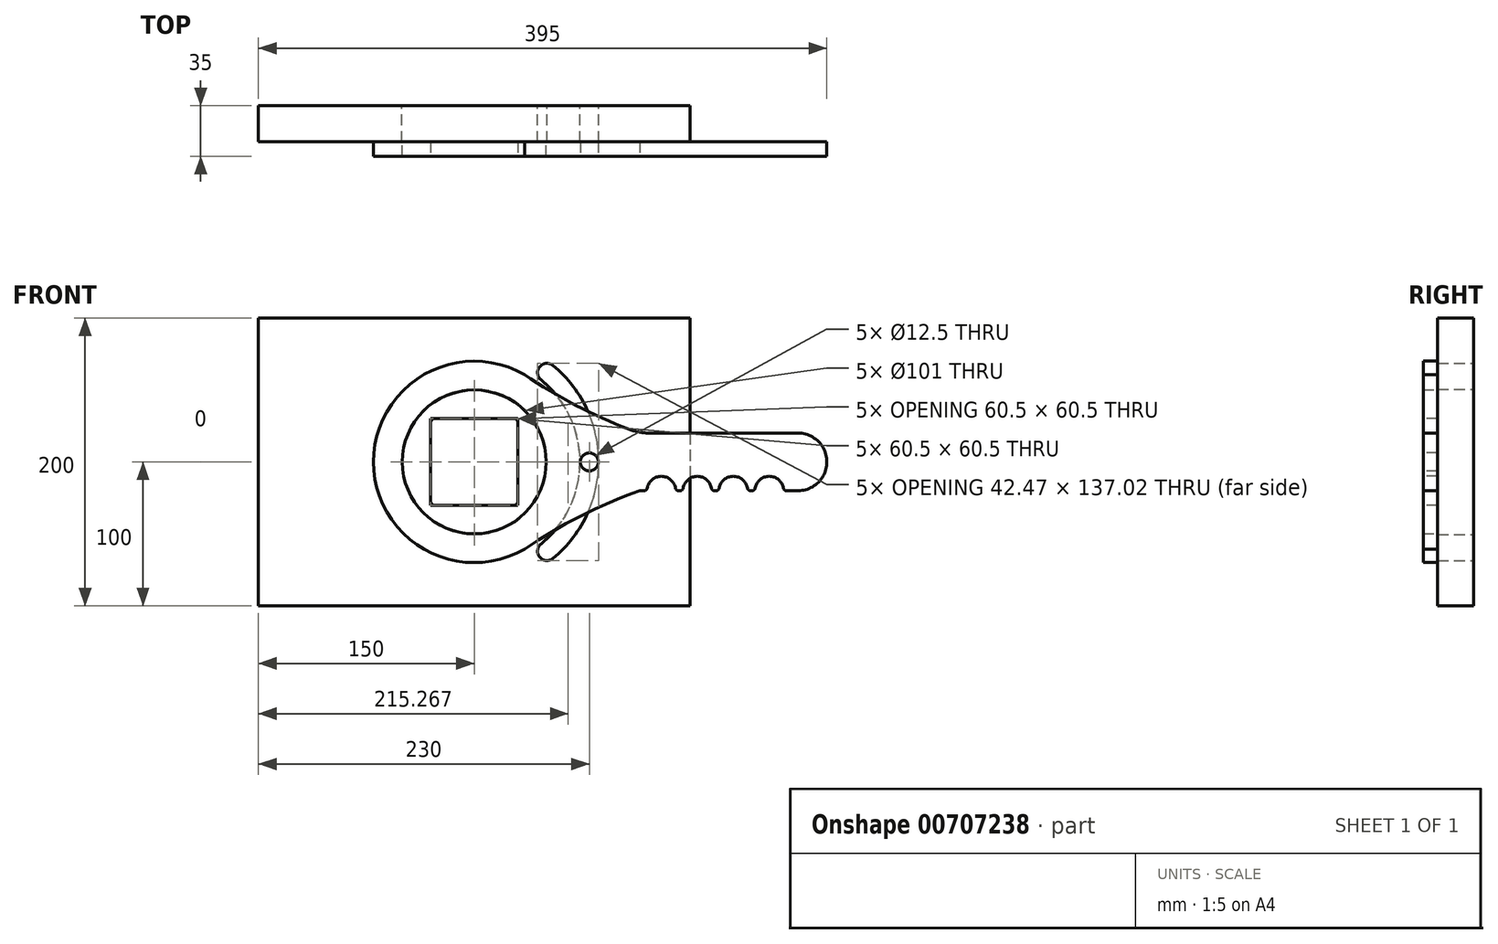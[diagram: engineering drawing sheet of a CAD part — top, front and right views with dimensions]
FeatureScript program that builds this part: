
annotation { "Feature Type Name" : "Feature", "Feature Type Description" : "" }
export const myFeature = defineFeature(function(context is Context, id is Id, definition is map)
    precondition{}
    {
        {
            var Q0;
            Q0=qCreatedBy(makeId("Front.planeOp"),FACE);
            var sketch = newSketch(context, id + "F0", { "sketchPlane" : qUnion([Q0])});
            skCircle(sketch, "E0.0", {"center": v(0, 0) * mm, "radius": 50.5 * mm});
            skLineSegment(sketch, "E1.bottom", {"start": v(150, 100) * mm, "end": v(-150, 100) * mm});
            skLineSegment(sketch, "E1.top", {"start": v(150, -100) * mm, "end": v(-150, -100) * mm});
            skLineSegment(sketch, "E1.left", {"start": v(150, 100) * mm, "end": v(150, -100) * mm});
            skLineSegment(sketch, "E1.right", {"start": v(-150, 100) * mm, "end": v(-150, -100) * mm});
            skArc(sketch, "E2", {"start": v(50.5, -62.05) * mm, "mid": v(80, 0) * mm, "end": v(50.5, 62.05) * mm, "construction": true});
            skLineSegment(sketch, "E3", {"start": v(50.5, 0) * mm, "end": v(50.5, 85.27) * mm, "construction": true});
            skLineSegment(sketch, "E4", {"start": v(50.5, 0) * mm, "end": v(50.5, -83.28) * mm, "construction": true});
            skArc(sketch, "E5.0.startCap", {"start": v(54.6, -67.09) * mm, "mid": v(45.46, -66.15) * mm, "end": v(46.4, -57) * mm});
            skArc(sketch, "E5.0.endCap", {"start": v(46.4, 57) * mm, "mid": v(45.46, 66.15) * mm, "end": v(54.6, 67.09) * mm});
            skArc(sketch, "E5.0.left", {"start": v(46.4, -57) * mm, "mid": v(73.5, 0) * mm, "end": v(46.4, 57) * mm});
            skArc(sketch, "E5.0.right", {"start": v(54.6, -67.09) * mm, "mid": v(86.5, 0) * mm, "end": v(54.6, 67.09) * mm});
            skSolve(sketch);
        }
        {
            var Q0;
            Q0=makeQuery(id+"F0.imprint","IMPRINT",FACE,{"disambiguationData":[TD([[makeQuery(id+"F0.imprint","IMPRINT",EDGE,{"derivedFrom":sQuery(id+"F0.wireOp",EDGE,"E0.0")}),-1.0]])]});
            extrude(context, id + "F1", {"entities" : qUnion([Q0]), "depth" : 25 * mm, "offsetDistance" : 25 * mm});
        }
        {
            var Q0;
            Q0=makeQuery(id+"F1.opExtrude","CAP_FACE",FACE,{"disambiguationData":[OSD([sQuery(id+"F0.wireOp",EDGE,"E0.0"),sQuery(id+"F0.wireOp",EDGE,"E1.bottom"),sQuery(id+"F0.wireOp",EDGE,"E1.top"),sQuery(id+"F0.wireOp",EDGE,"E1.left"),sQuery(id+"F0.wireOp",EDGE,"E1.right"),sQuery(id+"F0.wireOp",EDGE,"E5.0.startCap"),sQuery(id+"F0.wireOp",EDGE,"E5.0.endCap"),sQuery(id+"F0.wireOp",EDGE,"E5.0.left"),sQuery(id+"F0.wireOp",EDGE,"E5.0.right")])],"isStart":false});
            var sketch = newSketch(context, id + "F2", { "sketchPlane" : qUnion([Q0])});
            skPoint(sketch, "E6", {"position": v(0, 0) * mm});
            skCircle(sketch, "E7", {"center": v(0, 0) * mm, "radius": 50 * mm});
            skLineSegment(sketch, "E8.bottom", {"start": v(30.25, 30.25) * mm, "end": v(-30.25, 30.25) * mm});
            skLineSegment(sketch, "E8.top", {"start": v(30.25, -30.25) * mm, "end": v(-30.25, -30.25) * mm});
            skLineSegment(sketch, "E8.left", {"start": v(30.25, 30.25) * mm, "end": v(30.25, -30.25) * mm});
            skLineSegment(sketch, "E8.right", {"start": v(-30.25, 30.25) * mm, "end": v(-30.25, -30.25) * mm});
            skSolve(sketch);
        }
        {
            var Q0;
            Q0 = qSketchRegion(id + "F2", true);
            extrude(context, id + "F3", {"entities" : qUnion([Q0]), "depth" : 10 * mm, "offsetDistance" : 25 * mm});
        }
        {
            var Q0;
            Q0=makeQuery(id+"F3.opExtrude","CAP_FACE",FACE,{"disambiguationData":[OSD([sQuery(id+"F2.wireOp",EDGE,"E7"),sQuery(id+"F2.wireOp",EDGE,"E8.bottom"),sQuery(id+"F2.wireOp",EDGE,"E8.top"),sQuery(id+"F2.wireOp",EDGE,"E8.left"),sQuery(id+"F2.wireOp",EDGE,"E8.right")])],"isStart":false});
            var sketch = newSketch(context, id + "F4", { "sketchPlane" : qUnion([Q0])});
            skLineSegment(sketch, "E9", {"start": v(0, 0) * mm, "end": v(115, 0) * mm, "construction": true});
            skPoint(sketch, "E10", {"position": v(80, 0) * mm});
            skCircle(sketch, "E11", {"center": v(80, 0) * mm, "radius": 6.25 * mm});
            skLineSegment(sketch, "E12", {"start": v(115, 0) * mm, "end": v(218.42, 0) * mm, "construction": true});
            skArc(sketch, "E13", {"start": v(225, -20) * mm, "mid": v(245, 0) * mm, "end": v(225, 20) * mm});
            skLineSegment(sketch, "E14", {"start": v(225, 20) * mm, "end": v(122.1, 20) * mm});
            skLineSegment(sketch, "E15", {"start": v(225, -20) * mm, "end": v(216.83, -20) * mm});
            skPoint(sketch, "E16.end.orphan", {"position": v(21.65, -55.96) * mm});
            skPoint(sketch, "E17.orphan", {"position": v(21.65, 56) * mm});
            skPoint(sketch, "E18.orphan", {"position": v(97.33, 20) * mm});
            skPoint(sketch, "E19.orphan", {"position": v(97.33, -20) * mm});
            skArc(sketch, "E20", {"start": v(214.86, -18.33) * mm, "mid": v(205, -10) * mm, "end": v(195.14, -18.33) * mm});
            skArc(sketch, "E21", {"start": v(189.86, -18.33) * mm, "mid": v(180, -10) * mm, "end": v(170.14, -18.33) * mm});
            skArc(sketch, "E22", {"start": v(164.86, -18.33) * mm, "mid": v(155, -10) * mm, "end": v(145.14, -18.33) * mm});
            skArc(sketch, "E23", {"start": v(139.86, -18.33) * mm, "mid": v(130, -10) * mm, "end": v(120.14, -18.33) * mm});
            skLineSegment(sketch, "E24.trimOffspring", {"start": v(193.17, -20) * mm, "end": v(191.83, -20) * mm});
            skLineSegment(sketch, "E25.trimOffspring", {"start": v(168.17, -20) * mm, "end": v(166.83, -20) * mm});
            skLineSegment(sketch, "E26.trimOffspring", {"start": v(143.17, -20) * mm, "end": v(141.83, -20) * mm});
            skLineSegment(sketch, "E27.trimOffspring", {"start": v(118.17, -20) * mm, "end": v(115, -20) * mm});
            skPoint(sketch, "E28.visualSharp", {"position": v(120, -20) * mm});
            skArc(sketch, "E28.filletArc", {"start": v(118.17, -20) * mm, "mid": v(119.46, -19.53) * mm, "end": v(120.14, -18.33) * mm});
            skPoint(sketch, "E29.visualSharp", {"position": v(140, -20) * mm});
            skArc(sketch, "E29.filletArc", {"start": v(139.86, -18.33) * mm, "mid": v(140.54, -19.53) * mm, "end": v(141.83, -20) * mm});
            skPoint(sketch, "E30.visualSharp", {"position": v(145, -20) * mm});
            skArc(sketch, "E30.filletArc", {"start": v(143.17, -20) * mm, "mid": v(144.46, -19.53) * mm, "end": v(145.14, -18.33) * mm});
            skPoint(sketch, "E31.visualSharp", {"position": v(165, -20) * mm});
            skArc(sketch, "E31.filletArc", {"start": v(164.86, -18.33) * mm, "mid": v(165.54, -19.53) * mm, "end": v(166.83, -20) * mm});
            skPoint(sketch, "E32.visualSharp", {"position": v(170, -20) * mm});
            skArc(sketch, "E32.filletArc", {"start": v(168.17, -20) * mm, "mid": v(169.46, -19.53) * mm, "end": v(170.14, -18.33) * mm});
            skPoint(sketch, "E33.visualSharp", {"position": v(190, -20) * mm});
            skArc(sketch, "E33.filletArc", {"start": v(189.86, -18.33) * mm, "mid": v(190.54, -19.53) * mm, "end": v(191.83, -20) * mm});
            skPoint(sketch, "E34.visualSharp", {"position": v(195, -20) * mm});
            skArc(sketch, "E34.filletArc", {"start": v(193.17, -20) * mm, "mid": v(194.46, -19.53) * mm, "end": v(195.14, -18.33) * mm});
            skPoint(sketch, "E35.visualSharp", {"position": v(215, -20) * mm});
            skArc(sketch, "E35.filletArc", {"start": v(214.86, -18.33) * mm, "mid": v(215.54, -19.53) * mm, "end": v(216.83, -20) * mm});
            skArc(sketch, "E36.trimOffspring", {"start": v(21.65, -55.96) * mm, "mid": v(21.65, -55.98) * mm, "end": v(21.65, -56) * mm});
            skArc(sketch, "E37", {"start": v(35, 60.62) * mm, "mid": v(-70, 0) * mm, "end": v(35, -60.62) * mm});
            skPoint(sketch, "E38.orphan", {"position": v(35, 48.73) * mm});
            skPoint(sketch, "E39.orphan", {"position": v(35, -48.73) * mm});
            skLineSegment(sketch, "E40", {"start": v(35, 72.19) * mm, "end": v(35, -79.92) * mm, "construction": true});
            skArc(sketch, "E41", {"start": v(35, 60.62) * mm, "mid": v(70.33, 39.46) * mm, "end": v(107.91, 22.6) * mm});
            skArc(sketch, "E42.MirrorCS", {"start": v(35, -60.62) * mm, "mid": v(73.7, -37.73) * mm, "end": v(115, -20) * mm});
            skLineSegment(sketch, "E43.bottom", {"start": v(27.25, 30.25) * mm, "end": v(-27.25, 30.25) * mm});
            skLineSegment(sketch, "E43.top", {"start": v(27.25, -30.25) * mm, "end": v(-27.25, -30.25) * mm});
            skLineSegment(sketch, "E43.left", {"start": v(30.25, 27.25) * mm, "end": v(30.25, -27.25) * mm});
            skLineSegment(sketch, "E43.right", {"start": v(-30.25, 27.25) * mm, "end": v(-30.25, -27.25) * mm});
            skPoint(sketch, "E44.visualSharp", {"position": v(115, 20) * mm});
            skArc(sketch, "E44.filletArc", {"start": v(107.91, 22.6) * mm, "mid": v(114.9, 20.66) * mm, "end": v(122.1, 20) * mm});
            skPoint(sketch, "E45.visualSharp", {"position": v(-30.25, 30.25) * mm});
            skArc(sketch, "E45.filletArc", {"start": v(-27.25, 30.25) * mm, "mid": v(-29.37, 29.37) * mm, "end": v(-30.25, 27.25) * mm});
            skPoint(sketch, "E46.visualSharp", {"position": v(30.25, 30.25) * mm});
            skArc(sketch, "E46.filletArc", {"start": v(30.25, 27.25) * mm, "mid": v(29.37, 29.37) * mm, "end": v(27.25, 30.25) * mm});
            skPoint(sketch, "E47.visualSharp", {"position": v(30.25, -30.25) * mm});
            skArc(sketch, "E47.filletArc", {"start": v(27.25, -30.25) * mm, "mid": v(29.37, -29.37) * mm, "end": v(30.25, -27.25) * mm});
            skPoint(sketch, "E48.visualSharp", {"position": v(-30.25, -30.25) * mm});
            skArc(sketch, "E48.filletArc", {"start": v(-30.25, -27.25) * mm, "mid": v(-29.37, -29.37) * mm, "end": v(-27.25, -30.25) * mm});
            skSolve(sketch);
        }
        {
            var Q0;
            Q0 = qSketchRegion(id + "F4", true);
            extrude(context, id + "F5", {"entities" : qUnion([Q0]), "oppositeDirection" : true, "depth" : 10 * mm, "offsetDistance" : 25 * mm});
        }
    });
